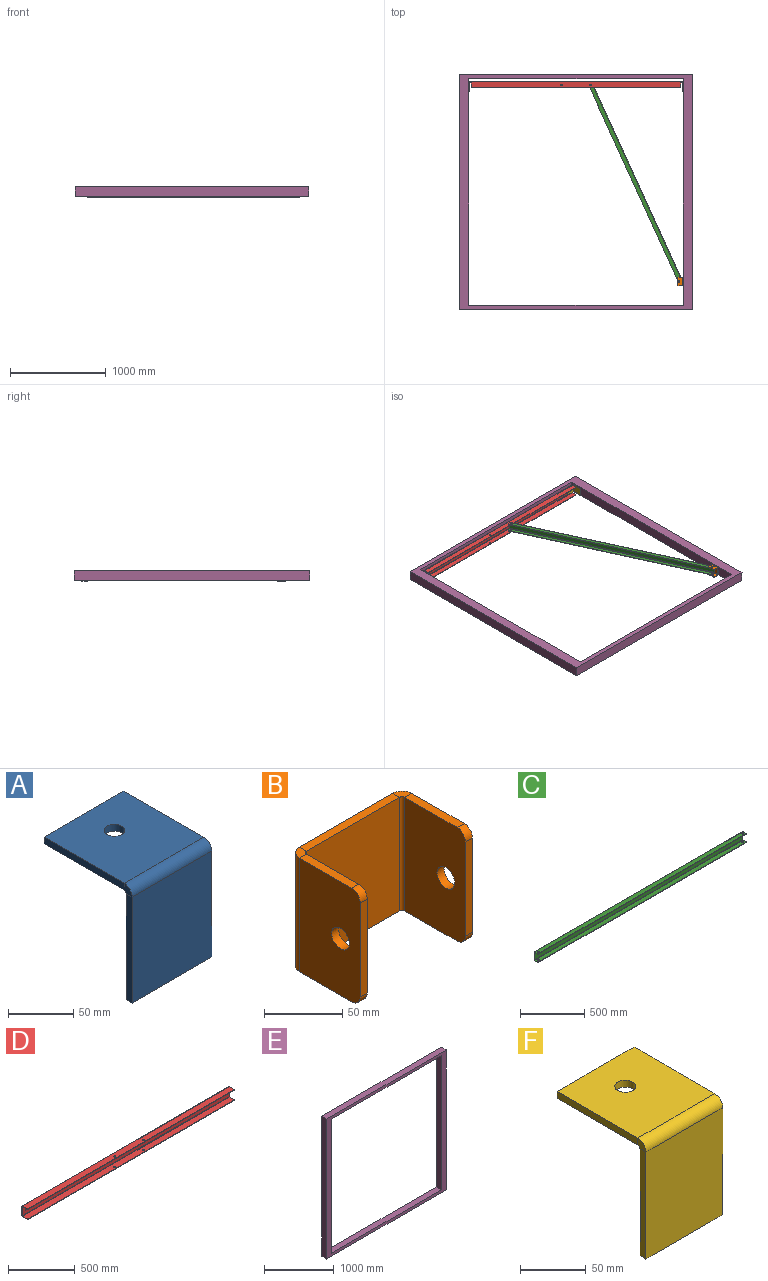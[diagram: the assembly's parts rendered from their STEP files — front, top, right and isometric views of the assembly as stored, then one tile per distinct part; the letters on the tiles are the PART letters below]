
ASSEMBLY  parts=6 mates=5
PART A: 15 faces, bbox 86.4x95.3x108 mm
  f0: plane 86.61x6.35mm, normal (1,0,0), area 550mm2, adj f1,f4,f5,f11
  f1: plane 86.36x6.35mm, normal (0,1,0), area 548.4mm2, adj f0,f3,f4,f5
  f2: cylinder r=7.94mm len=15.88mm, axis (0,0,1), area 316.7mm2, adj f4,f5
  f3: plane 86.61x6.35mm, normal (-1,0,0), area 550mm2, adj f1,f4,f5,f12
  f4: plane 86.61x86.36mm, normal (0,0,1), area 7282.1mm2, adj f0,f1,f2,f3,f13
  f5: plane 86.61x86.36mm, normal (0,0,-1), area 7282.1mm2, adj f0,f1,f2,f3,f14
  f6: plane 86.36x6.35mm, normal (0,0,-1), area 548.4mm2, adj f7,f8,f9,f10
  f7: plane 99.31x6.35mm, normal (1,0,0), area 630.6mm2, adj f6,f9,f10,f11
  f8: plane 99.31x6.35mm, normal (-1,0,0), area 630.6mm2, adj f6,f9,f10,f12
  f9: plane 99.31x86.36mm, normal (0,-1,0), area 8576.8mm2, adj f6,f7,f8,f13
  f10: plane 99.31x86.36mm, normal (0,1,0), area 8576.8mm2, adj f6,f7,f8,f14
  f11: plane 8.64x8.64mm, normal (1,0,0), area 54.5mm2, adj f0,f7,f13,f14
  f12: plane 8.64x8.64mm, normal (-1,0,0), area 54.5mm2, adj f3,f8,f13,f14
  f13: cylinder r=8.64mm len=86.36mm, axis (1,0,0), area 1171.5mm2, adj f4,f9,f11,f12
  f14: cylinder r=2.29mm len=86.36mm, axis (1,0,0), area 310.1mm2, adj f5,f10,f11,f12
PART B: 28 faces, bbox 101.6x63.5x88.9 mm
  f0: plane 84.33x6.35mm, normal (0,0,-1), area 535.5mm2, adj f2,f3,f12,f24
  f1: plane 84.33x6.35mm, normal (0,0,1), area 535.5mm2, adj f2,f3,f13,f25
  f2: plane 88.9x84.33mm, normal (0,1,0), area 7496.8mm2, adj f0,f1,f14,f26
  f3: plane 88.9x84.33mm, normal (0,-1,0), area 7496.8mm2, adj f0,f1,f15,f27
  f4: plane 73.66x6.35mm, normal (0,-1,0), area 467.7mm2, adj f8,f9,f10,f11
  f5: plane 47.24x6.35mm, normal (0,0,1), area 300mm2, adj f8,f9,f11,f13
  f6: cylinder r=8mm len=16mm, axis (-1,0,0), area 319.2mm2, adj f8,f9
  f7: plane 47.24x6.35mm, normal (0,0,-1), area 300mm2, adj f8,f9,f10,f12
  f8: plane 88.9x54.86mm, normal (-1,0,0), area 4651.4mm2, adj f4,f5,f6,f7,f10,f11,f14
  f9: plane 88.9x54.86mm, normal (1,0,0), area 4651.4mm2, adj f4,f5,f6,f7,f10,f11,f15
  f10: cylinder r=7.62mm len=7.62mm, axis (-1,0,0), area 76mm2, adj f4,f7,f8,f9
  f11: cylinder r=7.62mm len=7.62mm, axis (-1,0,0), area 76mm2, adj f4,f5,f8,f9
  f12: plane 8.64x8.64mm, normal (0,0,-1), area 54.5mm2, adj f0,f7,f14,f15
  f13: plane 8.64x8.64mm, normal (0,0,1), area 54.5mm2, adj f1,f5,f14,f15
  f14: cylinder r=8.64mm len=88.9mm, axis (0,0,-1), area 1206mm2, adj f2,f8,f12,f13
  f15: cylinder r=2.29mm len=88.9mm, axis (0,0,-1), area 319.2mm2, adj f3,f9,f12,f13
  f16: plane 73.66x6.35mm, normal (0,-1,0), area 467.7mm2, adj f20,f21,f22,f23
  f17: plane 47.24x6.35mm, normal (0,0,-1), area 300mm2, adj f20,f21,f22,f24
  f18: cylinder r=8mm len=16mm, axis (1,0,0), area 319.2mm2, adj f20,f21
  f19: plane 47.24x6.35mm, normal (0,0,1), area 300mm2, adj f20,f21,f23,f25
  f20: plane 88.9x54.86mm, normal (1,0,0), area 4651.4mm2, adj f16,f17,f18,f19,f22,f23,f26
  f21: plane 88.9x54.86mm, normal (-1,0,0), area 4651.4mm2, adj f16,f17,f18,f19,f22,f23,f27
  f22: cylinder r=7.62mm len=7.62mm, axis (1,0,0), area 76mm2, adj f16,f17,f20,f21
  f23: cylinder r=7.62mm len=7.62mm, axis (1,0,0), area 76mm2, adj f16,f19,f20,f21
  f24: plane 8.64x8.64mm, normal (0,0,-1), area 54.5mm2, adj f0,f17,f26,f27
  f25: plane 8.64x8.64mm, normal (0,0,1), area 54.5mm2, adj f1,f19,f26,f27
  f26: cylinder r=8.64mm len=88.9mm, axis (0,0,-1), area 1206mm2, adj f2,f20,f24,f25
  f27: cylinder r=2.29mm len=88.9mm, axis (0,0,-1), area 319.2mm2, adj f3,f21,f24,f25
PART C: 30 faces, bbox 2286x44.5x85.8 mm
  f0: plane 71.63x4.78mm, normal (-1,0,0), area 342mm2, adj f2,f3,f14,f27
  f1: plane 71.63x4.78mm, normal (1,0,0), area 342mm2, adj f2,f3,f13,f26
  f2: plane 2286x71.63mm, normal (0,1,0), area 163741.6mm2, adj f0,f1,f15,f28
  f3: plane 2286x71.63mm, normal (0,-1,0), area 163741.6mm2, adj f0,f1,f16,f29
  f4: plane 2269.49x4.78mm, normal (0,-1,0), area 10837.3mm2, adj f9,f10,f11,f12
  f5: plane 29.13x4.78mm, normal (1,0,0), area 139.1mm2, adj f9,f10,f12,f13
  f6: cylinder r=8mm len=16mm, axis (0,0,1), area 240.1mm2, adj f9,f10
  f7: cylinder r=8mm len=16mm, axis (0,0,1), area 240.1mm2, adj f9,f10
  f8: plane 29.13x4.78mm, normal (-1,0,0), area 139.1mm2, adj f9,f10,f11,f14
  f9: plane 2286x37.39mm, normal (0,0,1), area 85039.3mm2, adj f4,f5,f6,f7,f8,f11,f12,f15
  f10: plane 2286x37.39mm, normal (0,0,-1), area 85039.3mm2, adj f4,f5,f6,f7,f8,f11,f12,f16
  f11: cylinder r=8.26mm len=8.26mm, axis (0,0,1), area 61.9mm2, adj f4,f8,f9,f10
  f12: cylinder r=8.26mm len=8.26mm, axis (0,0,1), area 61.9mm2, adj f4,f5,f9,f10
  f13: plane 7.06x7.06mm, normal (1,0,0), area 35.1mm2, adj f1,f5,f15,f16
  f14: plane 7.06x7.06mm, normal (-1,0,0), area 35.1mm2, adj f0,f8,f15,f16
  f15: cylinder r=7.06mm len=2286mm, axis (1,0,0), area 25355.6mm2, adj f2,f9,f13,f14
  f16: cylinder r=2.29mm len=2286mm, axis (1,0,0), area 8208.7mm2, adj f3,f10,f13,f14
  f17: plane 2269.49x4.78mm, normal (0,-1,0), area 10837.3mm2, adj f22,f23,f24,f25
  f18: plane 29.13x4.78mm, normal (-1,0,0), area 139.1mm2, adj f22,f23,f24,f27
  f19: cylinder r=8mm len=16mm, axis (0,0,-1), area 240.1mm2, adj f22,f23
  f20: cylinder r=8mm len=16mm, axis (0,0,-1), area 240.1mm2, adj f22,f23
  f21: plane 29.13x4.78mm, normal (1,0,0), area 139.1mm2, adj f22,f23,f25,f26
  f22: plane 2286x37.39mm, normal (0,0,-1), area 85039.3mm2, adj f17,f18,f19,f20,f21,f24,f25,f28
  f23: plane 2286x37.39mm, normal (0,0,1), area 85039.3mm2, adj f17,f18,f19,f20,f21,f24,f25,f29
  f24: cylinder r=8.26mm len=8.26mm, axis (0,0,-1), area 61.9mm2, adj f17,f18,f22,f23
  f25: cylinder r=8.26mm len=8.26mm, axis (0,0,-1), area 61.9mm2, adj f17,f21,f22,f23
  f26: plane 7.06x7.06mm, normal (1,0,0), area 35.1mm2, adj f1,f21,f28,f29
  f27: plane 7.06x7.06mm, normal (-1,0,0), area 35.1mm2, adj f0,f18,f28,f29
  f28: cylinder r=7.06mm len=2286mm, axis (1,0,0), area 25355.6mm2, adj f2,f22,f26,f27
  f29: cylinder r=2.29mm len=2286mm, axis (1,0,0), area 8208.7mm2, adj f3,f23,f26,f27
PART D: 32 faces, bbox 2184.4x61.9x98.4 mm
  f0: plane 2167.89x4.76mm, normal (0,-1,0), area 10324.6mm2, adj f5,f6,f7,f8
  f1: plane 46.61x4.76mm, normal (1,0,0), area 222mm2, adj f5,f6,f7,f28
  f2: cylinder r=8mm len=16mm, axis (0,0,1), area 239.4mm2, adj f5,f6
  f3: cylinder r=8mm len=16mm, axis (0,0,1), area 239.4mm2, adj f5,f6
  f4: plane 46.61x4.76mm, normal (-1,0,0), area 222mm2, adj f5,f6,f8,f29
  f5: plane 2184.4x54.86mm, normal (0,0,1), area 119413.4mm2, adj f0,f1,f2,f3,f4,f7,f8,f30
  f6: plane 2184.4x54.86mm, normal (0,0,-1), area 119413.4mm2, adj f0,f1,f2,f3,f4,f7,f8,f31
  f7: cylinder r=8.26mm len=8.26mm, axis (0,0,1), area 61.8mm2, adj f0,f1,f5,f6
  f8: cylinder r=8.26mm len=8.26mm, axis (0,0,-1), area 61.8mm2, adj f0,f4,f5,f6
  f9: plane 84.33x4.76mm, normal (-1,0,0), area 401.6mm2, adj f13,f14,f25,f29
  f10: cylinder r=7.94mm len=15.88mm, axis (0,-1,0), area 237.5mm2, adj f13,f14
  f11: cylinder r=7.94mm len=15.88mm, axis (0,-1,0), area 237.5mm2, adj f13,f14
  f12: plane 84.33x4.76mm, normal (1,0,0), area 401.6mm2, adj f13,f14,f24,f28
  f13: plane 2184.4x84.33mm, normal (0,1,0), area 183810.2mm2, adj f9,f10,f11,f12,f26,f30
  f14: plane 2184.4x84.33mm, normal (0,-1,0), area 183810.2mm2, adj f9,f10,f11,f12,f27,f31
  f15: plane 2167.89x4.76mm, normal (0,-1,0), area 10324.6mm2, adj f20,f21,f22,f23
  f16: plane 46.61x4.76mm, normal (-1,0,0), area 222mm2, adj f20,f21,f22,f25
  f17: cylinder r=8mm len=16mm, axis (0,0,1), area 239.4mm2, adj f20,f21
  f18: cylinder r=8mm len=16mm, axis (0,0,1), area 239.4mm2, adj f20,f21
  f19: plane 46.61x4.76mm, normal (1,0,0), area 222mm2, adj f20,f21,f23,f24
  f20: plane 2184.4x54.86mm, normal (0,0,-1), area 119413.4mm2, adj f15,f16,f17,f18,f19,f22,f23,f26
  f21: plane 2184.4x54.86mm, normal (0,0,1), area 119413.4mm2, adj f15,f16,f17,f18,f19,f22,f23,f27
  f22: cylinder r=8.26mm len=8.26mm, axis (0,0,1), area 61.8mm2, adj f15,f16,f20,f21
  f23: cylinder r=8.26mm len=8.26mm, axis (0,0,-1), area 61.8mm2, adj f15,f19,f20,f21
  f24: plane 7.05x7.05mm, normal (1,0,0), area 34.9mm2, adj f12,f19,f26,f27
  f25: plane 7.05x7.05mm, normal (-1,0,0), area 34.9mm2, adj f9,f16,f26,f27
  f26: cylinder r=7.05mm len=2184.4mm, axis (1,0,0), area 24185.1mm2, adj f13,f20,f24,f25
  f27: cylinder r=2.29mm len=2184.4mm, axis (1,0,0), area 7843.8mm2, adj f14,f21,f24,f25
  f28: plane 7.05x7.05mm, normal (1,0,0), area 34.9mm2, adj f1,f12,f30,f31
  f29: plane 7.05x7.05mm, normal (-1,0,0), area 34.9mm2, adj f4,f9,f30,f31
  f30: cylinder r=7.05mm len=2184.4mm, axis (1,0,0), area 24185.1mm2, adj f5,f13,f28,f29
  f31: cylinder r=2.29mm len=2184.4mm, axis (1,0,0), area 7843.8mm2, adj f6,f14,f28,f29
PART E: 10 faces, bbox 2438.4x101.6x2462.2 mm
  f0: plane 2462.18x101.6mm, normal (-1,0,0), area 250157.1mm2, adj f1,f7,f8,f9
  f1: plane 2438.4x101.6mm, normal (0,0,-1), area 247741.4mm2, adj f0,f2,f8,f9
  f2: plane 2462.18x101.6mm, normal (1,0,0), area 250157.1mm2, adj f1,f7,f8,f9
  f3: plane 2360.58x101.6mm, normal (-1,0,0), area 239834.6mm2, adj f4,f6,f8,f9
  f4: plane 2235.2x101.6mm, normal (0,0,1), area 227096.3mm2, adj f3,f5,f8,f9
  f5: plane 2360.58x101.6mm, normal (1,0,0), area 239834.6mm2, adj f4,f6,f8,f9
  f6: plane 2235.2x101.6mm, normal (0,0,-1), area 227096.3mm2, adj f3,f5,f8,f9
  f7: plane 2438.4x101.6mm, normal (0,0,1), area 247741.4mm2, adj f0,f2,f8,f9
  f8: plane 2462.18x2438.4mm, normal (0,-1,0), area 727410.6mm2, adj f0,f1,f2,f3,f4,f5,f6,f7
  f9: plane 2462.18x2438.4mm, normal (0,1,0), area 727410.6mm2, adj f0,f1,f2,f3,f4,f5,f6,f7
PART F: 15 faces, bbox 82.6x95.3x108 mm
  f0: plane 86.61x6.35mm, normal (1,0,0), area 550mm2, adj f1,f4,f5,f11
  f1: plane 82.55x6.35mm, normal (0,1,0), area 524.2mm2, adj f0,f3,f4,f5
  f2: cylinder r=7.94mm len=15.88mm, axis (0,0,1), area 316.7mm2, adj f4,f5
  f3: plane 86.61x6.35mm, normal (-1,0,0), area 550mm2, adj f1,f4,f5,f12
  f4: plane 86.61x82.55mm, normal (0,0,1), area 6952.1mm2, adj f0,f1,f2,f3,f13
  f5: plane 86.61x82.55mm, normal (0,0,-1), area 6952.1mm2, adj f0,f1,f2,f3,f14
  f6: plane 82.55x6.35mm, normal (0,0,-1), area 524.2mm2, adj f7,f8,f9,f10
  f7: plane 99.31x6.35mm, normal (1,0,0), area 630.6mm2, adj f6,f9,f10,f11
  f8: plane 99.31x6.35mm, normal (-1,0,0), area 630.6mm2, adj f6,f9,f10,f12
  f9: plane 99.31x82.55mm, normal (0,-1,0), area 8198.4mm2, adj f6,f7,f8,f13
  f10: plane 99.31x82.55mm, normal (0,1,0), area 8198.4mm2, adj f6,f7,f8,f14
  f11: plane 8.64x8.64mm, normal (1,0,0), area 54.5mm2, adj f0,f7,f13,f14
  f12: plane 8.64x8.64mm, normal (-1,0,0), area 54.5mm2, adj f3,f8,f13,f14
  f13: cylinder r=8.64mm len=82.55mm, axis (1,0,0), area 1119.8mm2, adj f4,f9,f11,f12
  f14: cylinder r=2.29mm len=82.55mm, axis (1,0,0), area 296.4mm2, adj f5,f10,f11,f12
PLACE A rot(axis=(-0.58,-0.58,-0.58),120deg) t=(-2530.57,1269.39,1380.04)mm
PLACE B rot(axis=(-0.58,-0.58,-0.58),120deg) t=(-388,-750.92,1376.05)mm
PLACE C rot(axis=(0,0,-1),65.5deg) t=(-1059.23,704.73,1288.47)mm
PLACE D rot(axis=(0.11,0.96,0.27),0deg) t=(-1411.95,1331.57,1365.65)mm
PLACE E rot(axis=(-1,0,0),90deg) t=(-1482.37,-290.97,1276.69)mm
PLACE F rot(axis=(-0.58,0.58,0.58),120deg) t=(-485.87,1269.39,1253.03)mm
MATE planar E.f5 <-> A.f9  axis (1,0,0) through (-2625.82,179.57,1327.49)mm
MATE fastened D.f11 <-> A.f2  axis (0,-1,0) through (-2562.32,1331.57,1318.12)mm
MATE fastened F.f2 <-> D.f10  axis (0,1,0) through (-454.12,1331.57,1318.12)mm
MATE pin_slot C.f20 <-> D.f3  axis (0,0,1) through (-1355.82,1294.29,1362.51)mm
MATE pin_slot B.f18 <-> C.f19  axis (0,0,-1) through (-433.72,-753.02,1362.51)mm
